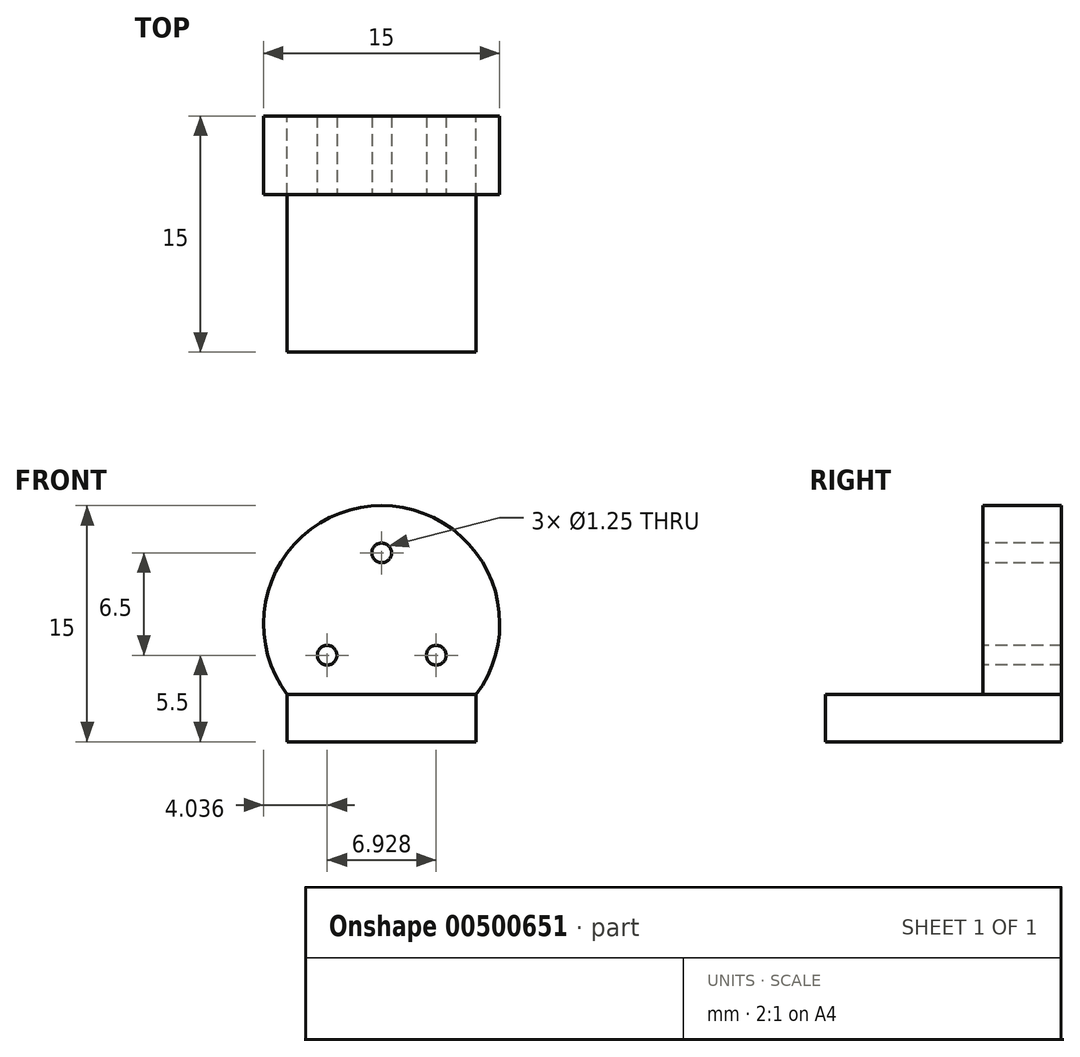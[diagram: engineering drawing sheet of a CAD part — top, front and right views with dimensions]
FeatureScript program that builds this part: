
annotation { "Feature Type Name" : "Feature", "Feature Type Description" : "" }
export const myFeature = defineFeature(function(context is Context, id is Id, definition is map)
    precondition{}
    {
        {
            var Q0;
            Q0=qCreatedBy(makeId("Front.planeOp"),FACE);
            var sketch = newSketch(context, id + "F0", { "sketchPlane" : qUnion([Q0])});
            skCircle(sketch, "E0", {"center": v(0, 0) * mm, "radius": 7.5 * mm});
            skLineSegment(sketch, "E1", {"start": v(0, 0) * mm, "end": v(0, 7.5) * mm});
            skLineSegment(sketch, "E2", {"start": v(0, 0) * mm, "end": v(-6.5, -3.75) * mm});
            skLineSegment(sketch, "E3", {"start": v(0, 0) * mm, "end": v(6.5, -3.75) * mm});
            skPoint(sketch, "E4", {"position": v(0, 4.5) * mm});
            skPoint(sketch, "E5", {"position": v(3.46, -2) * mm});
            skPoint(sketch, "E6", {"position": v(-3.46, -2) * mm});
            skLineSegment(sketch, "E7", {"start": v(0, -7.5) * mm, "end": v(-6, -7.5) * mm});
            skLineSegment(sketch, "E8", {"start": v(-6, -7.5) * mm, "end": v(-6, -4.5) * mm});
            skLineSegment(sketch, "E9", {"start": v(-6, -4.5) * mm, "end": v(6, -4.5) * mm});
            skLineSegment(sketch, "E10", {"start": v(6, -4.5) * mm, "end": v(6, -7.5) * mm});
            skLineSegment(sketch, "E11", {"start": v(6, -7.5) * mm, "end": v(0, -7.5) * mm});
            skSolve(sketch);
        }
        {
            var Q0;
            {var subQ0=sQuery(id+"F0.wireOp",EDGE,"E1");Q0=makeQuery(id+"F0.imprint","IMPRINT",FACE,{"disambiguationData":[TD([[makeQuery(id+"F0.imprint","IMPRINT",EDGE,{"derivedFrom":subQ0}),-1.0]])]});}
            var Q1;
            {var subQ0=sQuery(id+"F0.wireOp",EDGE,"E1");Q1=makeQuery(id+"F0.imprint","IMPRINT",FACE,{"disambiguationData":[TD([[makeQuery(id+"F0.imprint","IMPRINT",EDGE,{"derivedFrom":subQ0}),1.0]])]});}
            var Q2;
            {var subQ1=sQuery(id+"F0.wireOp",EDGE,"E2");Q2=makeQuery(id+"F0.imprint","IMPRINT",FACE,{"disambiguationData":[TD([[makeQuery(id+"F0.imprint","IMPRINT",EDGE,{"derivedFrom":subQ1}),1.0]])]});}
            extrude(context, id + "F1", {"entities" : qUnion([Q0, Q1, Q2]), "depth" : 5 * mm});
        }
        {
            var Q0;
            {var subQ2=sQuery(id+"F0.wireOp",EDGE,"E9");Q0=makeQuery(id+"F0.imprint","IMPRINT",FACE,{"disambiguationData":[TD([[makeQuery(id+"F0.imprint","IMPRINT",EDGE,{"derivedFrom":subQ2}),-1.0]])]});}
            var Q1;
            {var subQ2=sQuery(id+"F0.wireOp",EDGE,"E10");Q1=makeQuery(id+"F0.imprint","IMPRINT",FACE,{"disambiguationData":[TD([[makeQuery(id+"F0.imprint","IMPRINT",EDGE,{"derivedFrom":subQ2}),-1.0]])]});}
            var Q2;
            {var subQ0=sQuery(id+"F0.wireOp",EDGE,"E7");Q2=makeQuery(id+"F0.imprint","IMPRINT",FACE,{"disambiguationData":[TD([[makeQuery(id+"F0.imprint","IMPRINT",EDGE,{"derivedFrom":subQ0}),-1.0]])]});}
            extrude(context, id + "F2", {"entities" : qUnion([Q0, Q1, Q2]), "operationType" : NewBodyOperationType.ADD, "depth" : 15 * mm});
        }
        {
            var Q0;
            Q0=sQuery(id+"F0.wireOp",VERTEX,"E5");
            var Q1;
            Q1=sQuery(id+"F0.wireOp",VERTEX,"E6");
            var Q2;
            Q2=sQuery(id+"F0.wireOp",VERTEX,"E4");
            var Q3;
            Q3=makeQuery(id+"F1.opExtrude","SWEPT_BODY",BODY,{"disambiguationData":[OSD([sQuery(id+"F0.wireOp",EDGE,"E0"),sQuery(id+"F0.wireOp",EDGE,"E9")])]});
            hole(context, id + "F3", {"style" : HoleStyle.SIMPLE, "endStyle" : HoleEndStyle.THROUGH, "oppositeDirection" : true, "holeDiameter" : 1.25 * mm, "isTappedThrough" : true, "tappedDepth" : 12 * mm, "tapClearance" : 3, "locations" : qUnion([Q0, Q1, Q2]), "scope" : qUnion([Q3]), "startStyle" : HoleStartStyle.SKETCH});
        }
    });
